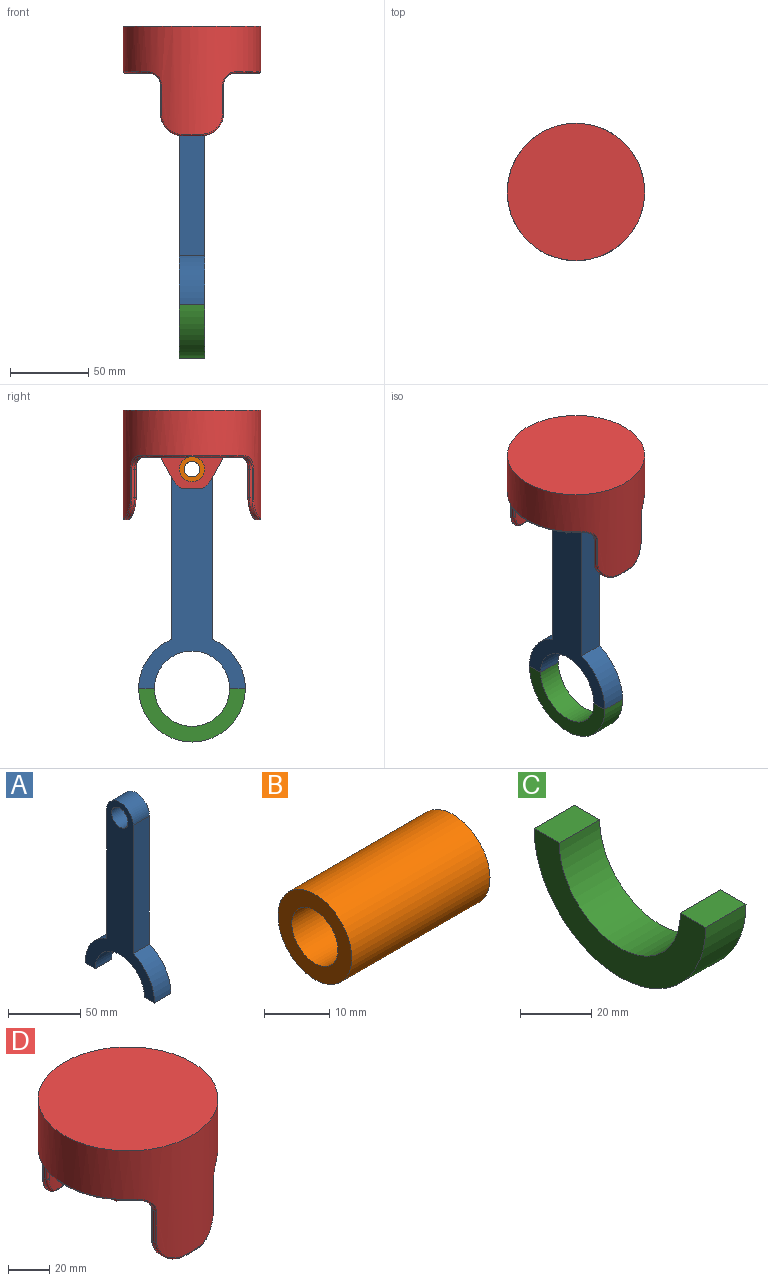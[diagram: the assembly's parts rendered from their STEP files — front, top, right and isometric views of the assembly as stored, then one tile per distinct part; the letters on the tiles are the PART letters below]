
ASSEMBLY  parts=4 mates=3
PART A: 11 faces, bbox 16x68x153 mm
  f0: cylinder r=13mm len=26mm, axis (-1,0,0), area 653.5mm2, adj f1,f8,f9,f10
  f1: plane 108.58x16mm, normal (0,-1,0), area 1737.3mm2, adj f0,f2,f9,f10
  f2: cylinder r=34mm len=31.42mm, axis (-1,0,0), area 641.1mm2, adj f1,f3,f9,f10
  f3: plane 16x10mm, normal (0,0,-1), area 160mm2, adj f2,f4,f9,f10
  f4: cylinder r=24mm len=48mm, axis (-1,0,0), area 1206.4mm2, adj f3,f5,f9,f10
  f5: plane 16x10mm, normal (0,0,-1), area 160mm2, adj f4,f6,f9,f10
  f6: cylinder r=34mm len=31.42mm, axis (-1,0,0), area 641.1mm2, adj f5,f8,f9,f10
  f7: cylinder r=8mm len=16mm, axis (-1,0,0), area 804.2mm2, adj f9,f10
  f8: plane 108.58x16mm, normal (0,1,0), area 1737.3mm2, adj f0,f6,f9,f10
  f9: plane 153x68mm, normal (1,0,0), area 3753.5mm2, adj f0,f1,f2,f3,f4,f5,f6,f7
  f10: plane 153x68mm, normal (-1,0,0), area 3753.5mm2, adj f0,f1,f2,f3,f4,f5,f6,f7
PART B: 4 faces, bbox 30x16x16 mm
  f0: cylinder r=5mm len=30mm, axis (-1,0,0), area 942.5mm2, adj f2,f3
  f1: cylinder r=8mm len=30mm, axis (-1,0,0), area 1508mm2, adj f2,f3
  f2: plane 16x16mm, normal (1,0,0), area 122.5mm2, adj f0,f1
  f3: plane 16x16mm, normal (-1,0,0), area 122.5mm2, adj f0,f1
PART C: 6 faces, bbox 16x68x34 mm
  f0: plane 16x10mm, normal (0,0,1), area 160mm2, adj f1,f3,f4,f5
  f1: cylinder r=24mm len=48mm, axis (-1,0,0), area 1206.4mm2, adj f0,f2,f4,f5
  f2: plane 16x10mm, normal (0,0,1), area 160mm2, adj f1,f3,f4,f5
  f3: cylinder r=34mm len=68mm, axis (-1,0,0), area 1709mm2, adj f0,f2,f4,f5
  f4: plane 68x34mm, normal (1,0,0), area 911.1mm2, adj f0,f1,f2,f3
  f5: plane 68x34mm, normal (-1,0,0), area 911.1mm2, adj f0,f1,f2,f3
PART D: 104 faces, bbox 94.8x88.5x70 mm
  f0: cylinder r=40.3mm len=80.61mm, axis (0,0,-1), area 6258.1mm2, adj f1,f3,f4,f5,f6,f8,f9,f10
  f1: plane 2.51x0.59mm, normal (0,0,-1), area 0.8mm2, adj f0,f4,f99
  f2: plane 13.43x7mm, normal (0,0,-1), area 94mm2, adj f4,f5,f96,f103
  f3: plane 2.51x0.59mm, normal (0,0,-1), area 0.8mm2, adj f0,f4,f91
  f4: plane 79.01x42mm, normal (1,0,0), area 1916.5mm2, adj f0,f1,f2,f3,f19,f20,f21,f71
  f5: plane 74.82x42mm, normal (-1,0,0), area 1817.2mm2, adj f0,f2,f22,f23,f71,f92,f93,f94
  f6: plane 2.51x0.59mm, normal (0,0,-1), area 0.8mm2, adj f0,f9,f86
  f7: plane 13.43x7mm, normal (0,0,-1), area 94mm2, adj f9,f10,f78,f85
  f8: plane 2.51x0.59mm, normal (0,0,-1), area 0.8mm2, adj f0,f9,f79
  f9: plane 79.01x42mm, normal (-1,0,0), area 1916.5mm2, adj f0,f6,f7,f8,f19,f20,f21,f70
  f10: plane 74.82x42mm, normal (1,0,0), area 1817.2mm2, adj f0,f7,f32,f41,f70,f74,f75,f76
  f11: plane 30.26x14.75mm, normal (0,0,-1), area 50mm2, adj f15,f17,f39,f73
  f12: plane 30.26x14.75mm, normal (0,0,-1), area 50mm2, adj f15,f17,f37,f73
  f13: plane 30.26x14.75mm, normal (0,0,-1), area 50mm2, adj f16,f18,f38,f72
  f14: plane 30.26x14.75mm, normal (0,0,-1), area 50mm2, adj f16,f18,f40,f72
  f15: torus R=42.8mm, axis (0,0,1), area 114.5mm2, adj f11,f12,f28,f42,f45,f73
  f16: torus R=42.8mm, axis (0,0,-1), area 114.5mm2, adj f13,f14,f28,f52,f55,f72
  f17: torus R=41.3mm, axis (0,0,1), area 103mm2, adj f0,f11,f12,f59,f62,f73
  f18: torus R=41.3mm, axis (0,0,-1), area 103mm2, adj f0,f13,f14,f63,f66,f72
  f19: plane 74.61x16mm, normal (0,0,-1), area 1184.5mm2, adj f4,f9,f20,f21
  f20: torus R=37.3mm, axis (0,0,-1), area 75.9mm2, adj f0,f4,f9,f19
  f21: torus R=37.3mm, axis (0,0,-1), area 75.9mm2, adj f0,f4,f9,f19
  f22: plane 68.31x22.3mm, normal (0,0,-1), area 1097.6mm2, adj f5,f23
  f23: torus R=37.3mm, axis (0,0,-1), area 435.5mm2, adj f0,f5,f22
  f24: plane 12x1.94mm, normal (0,0,-1), area 18.1mm2, adj f33,f34,f46,f58
  f25: plane 12x1.94mm, normal (0,0,-1), area 18.1mm2, adj f35,f36,f51,f67
  f26: plane 18x1.68mm, normal (1,0,0), area 30.3mm2, adj f36,f37,f47,f64
  f27: plane 18x1.68mm, normal (-1,0,0), area 30.3mm2, adj f35,f38,f54,f68
  f28: cylinder r=43.8mm len=87.61mm, axis (0,0,1), area 11126.3mm2, adj f15,f16,f29,f42,f43,f44,f45,f46
  f29: plane 87.61x87.61mm, normal (0,0,1), area 6027.8mm2, adj f28
  f30: plane 18x1.68mm, normal (1,0,0), area 30.3mm2, adj f33,f39,f43,f57
  f31: plane 18x1.68mm, normal (-1,0,0), area 30.3mm2, adj f34,f40,f50,f61
  f32: plane 68.31x22.3mm, normal (0,0,-1), area 1097.6mm2, adj f10,f41
  f33: cylinder r=14mm len=14mm, axis (0,-1,0), area 35.3mm2, adj f24,f30,f44,f56
  f34: cylinder r=14mm len=14mm, axis (0,1,0), area 35.3mm2, adj f24,f31,f48,f60
  f35: cylinder r=14mm len=14mm, axis (0,1,0), area 35.3mm2, adj f25,f27,f53,f69
  f36: cylinder r=14mm len=14mm, axis (0,-1,0), area 35.3mm2, adj f25,f26,f49,f65
  f37: cylinder r=8mm len=8mm, axis (0,-1,0), area 22.4mm2, adj f12,f26,f45,f62
  f38: cylinder r=8mm len=8mm, axis (0,-1,0), area 22.4mm2, adj f13,f27,f55,f66
  f39: cylinder r=8mm len=8mm, axis (0,-1,0), area 22.4mm2, adj f11,f30,f42,f59
  f40: cylinder r=8mm len=8mm, axis (0,-1,0), area 22.4mm2, adj f14,f31,f52,f63
  f41: torus R=37.3mm, axis (0,0,-1), area 435.5mm2, adj f0,f10,f32
  f42: bspline ~10.83x10.37mm, area 19mm2, adj f15,f28,f39,f43
  f43: cylinder r=1mm len=18mm, axis (0,0,1), area 20mm2, adj f28,f30,f42,f44
  f44: bspline ~15.51x14.38mm, area 29.1mm2, adj f28,f33,f43,f46
  f45: bspline ~10.37x9.47mm, area 19mm2, adj f15,f28,f37,f47
  f46: torus R=42.8mm, axis (0,0,1), area 19.2mm2, adj f24,f28,f44,f48
  f47: cylinder r=1mm len=18mm, axis (0,0,1), area 20mm2, adj f26,f28,f45,f49
  f48: bspline ~15.51x15.48mm, area 29.1mm2, adj f28,f34,f46,f50
  f49: bspline ~15.51x15.48mm, area 29.1mm2, adj f28,f36,f47,f51
  f50: cylinder r=1mm len=18mm, axis (0,0,1), area 20mm2, adj f28,f31,f48,f52
  f51: torus R=42.8mm, axis (0,0,1), area 19.2mm2, adj f25,f28,f49,f53
  f52: bspline ~10.37x9.47mm, area 19mm2, adj f16,f28,f40,f50
  f53: bspline ~15.51x14.38mm, area 29.1mm2, adj f28,f35,f51,f54
  f54: cylinder r=1mm len=18mm, axis (0,0,1), area 20mm2, adj f27,f28,f53,f55
  f55: bspline ~10.83x10.37mm, area 19mm2, adj f16,f28,f38,f54
  f56: bspline ~15.61x15.56mm, area 39.9mm2, adj f0,f33,f57,f58
  f57: cylinder r=1mm len=18mm, axis (0,0,-1), area 36.9mm2, adj f0,f30,f56,f59
  f58: torus R=41.3mm, axis (0,0,1), area 18.6mm2, adj f0,f24,f56,f60
  f59: bspline ~10.82x10.71mm, area 27.7mm2, adj f0,f17,f39,f57
  f60: bspline ~15.61x15.56mm, area 39.9mm2, adj f0,f34,f58,f61
  f61: cylinder r=1mm len=18mm, axis (0,0,-1), area 36.9mm2, adj f0,f31,f60,f63
  f62: bspline ~10.82x9.78mm, area 27.7mm2, adj f0,f17,f37,f64
  f63: bspline ~10.82x9.78mm, area 27.7mm2, adj f0,f18,f40,f61
  f64: cylinder r=1mm len=18mm, axis (0,0,-1), area 36.9mm2, adj f0,f26,f62,f65
  f65: bspline ~15.61x15.56mm, area 39.9mm2, adj f0,f36,f64,f67
  f66: bspline ~10.82x10.71mm, area 27.7mm2, adj f0,f18,f38,f68
  f67: torus R=41.3mm, axis (0,0,1), area 18.6mm2, adj f0,f25,f65,f69
  f68: cylinder r=1mm len=18mm, axis (0,0,-1), area 36.9mm2, adj f0,f27,f66,f69
  f69: bspline ~15.61x15.56mm, area 39.9mm2, adj f0,f35,f67,f68
  f70: cylinder r=8mm len=16mm, axis (-1,0,0), area 351.9mm2, adj f9,f10
  f71: cylinder r=8mm len=16mm, axis (-1,0,0), area 351.9mm2, adj f4,f5
  f72: cylinder r=8mm len=4.23mm, axis (-1,0,0), area 11.2mm2, adj f13,f14,f16,f18
  f73: cylinder r=8mm len=4.23mm, axis (-1,0,0), area 11.2mm2, adj f11,f12,f15,f17
  f74: plane 18.74x10.34mm, normal (0,0.88,-0.48), area 149.8mm2, adj f9,f10,f75,f78
  f75: cylinder r=5mm len=7mm, axis (1,0,0), area 37.3mm2, adj f9,f10,f74,f76
  f76: plane 7x6.93mm, normal (0,0,-1), area 48.5mm2, adj f9,f10,f75,f77
  f77: cylinder r=5mm len=8mm, axis (1,0,0), area 59.2mm2, adj f0,f9,f10,f76,f79,f80
  f78: cylinder r=14mm len=7mm, axis (1,0,0), area 55.5mm2, adj f7,f9,f10,f74
  f79: plane 24.1x8mm, normal (0,-1,0), area 187.2mm2, adj f0,f8,f9,f77,f80,f81
  f80: plane 28.04x1.92mm, normal (-1,0,0), area 51.5mm2, adj f0,f77,f79,f81
  f81: plane 5.49x1.92mm, normal (0,0.01,1), area 4.9mm2, adj f0,f79,f80
  f82: plane 11.93x8mm, normal (0,0,-1), area 85.2mm2, adj f0,f9,f10,f83,f86,f87
  f83: cylinder r=5mm len=7mm, axis (1,0,0), area 37.3mm2, adj f9,f10,f82,f84
  f84: plane 18.74x10.34mm, normal (0,-0.88,-0.48), area 149.8mm2, adj f9,f10,f83,f85
  f85: cylinder r=14mm len=7mm, axis (1,0,0), area 55.5mm2, adj f7,f9,f10,f84
  f86: plane 29.1x8mm, normal (0,1,0), area 227.2mm2, adj f0,f6,f9,f82,f87,f88
  f87: plane 29.1x1.92mm, normal (-1,0,0), area 55.8mm2, adj f0,f82,f86,f88
  f88: plane 5.49x1.92mm, normal (0,-0.01,1), area 4.9mm2, adj f0,f86,f87
  f89: plane 5.49x1.92mm, normal (0,0.01,1), area 4.9mm2, adj f0,f90,f91
  f90: plane 28.04x1.92mm, normal (1,0,0), area 51.5mm2, adj f0,f89,f91,f92
  f91: plane 24.1x8mm, normal (0,-1,0), area 187.2mm2, adj f0,f3,f4,f89,f90,f92
  f92: cylinder r=5mm len=8mm, axis (1,0,0), area 59.2mm2, adj f0,f4,f5,f90,f91,f93
  f93: plane 7x6.93mm, normal (0,0,-1), area 48.5mm2, adj f4,f5,f92,f94
  f94: cylinder r=5mm len=7mm, axis (1,0,0), area 37.3mm2, adj f4,f5,f93,f95
  f95: plane 18.74x10.34mm, normal (0,0.88,-0.48), area 149.8mm2, adj f4,f5,f94,f96
  f96: cylinder r=14mm len=7mm, axis (1,0,0), area 55.5mm2, adj f2,f4,f5,f95
  f97: plane 5.49x1.92mm, normal (0,-0.01,1), area 4.9mm2, adj f0,f98,f99
  f98: plane 29.1x1.92mm, normal (1,0,0), area 55.8mm2, adj f0,f97,f99,f102
  f99: plane 29.1x8mm, normal (0,1,0), area 227.2mm2, adj f0,f1,f4,f97,f98,f102
  f100: plane 18.74x10.34mm, normal (0,-0.88,-0.48), area 149.8mm2, adj f4,f5,f101,f103
  f101: cylinder r=5mm len=7mm, axis (1,0,0), area 37.3mm2, adj f4,f5,f100,f102
  f102: plane 11.93x8mm, normal (0,0,-1), area 85.2mm2, adj f0,f4,f5,f98,f99,f101
  f103: cylinder r=14mm len=7mm, axis (1,0,0), area 55.5mm2, adj f2,f4,f5,f100
PLACE A t=(-183.76,-75.08,-46.99)mm
PLACE B t=(-118.76,-75.08,26.03)mm
PLACE C t=(-183.76,-75.08,-36.9)mm
PLACE D t=(3.24,-75.08,21.87)mm
MATE revolute B.f0 <-> A.f0  axis (-1,0,0) through (3.24,-75.08,134.15)mm
MATE fastened A.f5 <-> C.f0  axis (0,0,-1) through (3.24,-46.08,-5.85)mm
MATE fastened B.f0 <-> D.f70  axis (1,0,0) through (18.24,-75.08,134.15)mm
